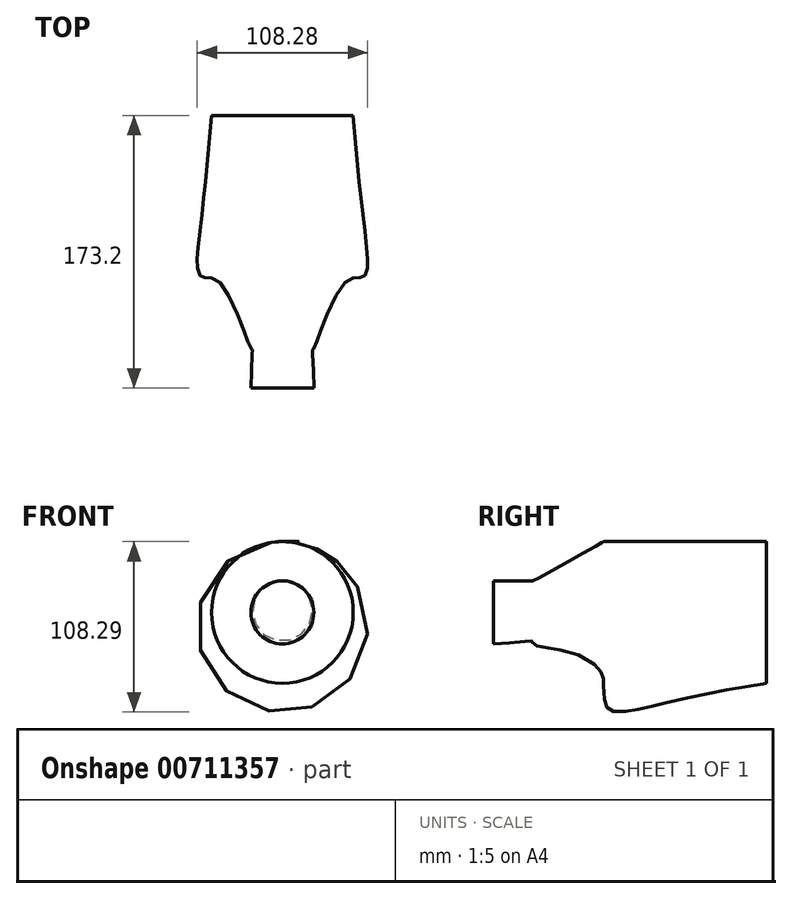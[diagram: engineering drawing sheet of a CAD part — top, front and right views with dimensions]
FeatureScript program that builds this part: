
annotation { "Feature Type Name" : "Feature", "Feature Type Description" : "" }
export const myFeature = defineFeature(function(context is Context, id is Id, definition is map)
    precondition{}
    {
        {
            var Q0;
            Q0=qCreatedBy(makeId("Front.planeOp"),FACE);
            var sketch = newSketch(context, id + "F0", { "sketchPlane" : qUnion([Q0])});
            skCircle(sketch, "E0", {"center": v(0, 45) * mm, "radius": 45 * mm});
            skSolve(sketch);
        }
        {
            var Q0;
            Q0=qCreatedBy(makeId("Front.planeOp"),FACE);
            cPlane(context, id + "F1", {"entities" : qUnion([Q0]), "cplaneType" : CPlaneType.OFFSET, "offset" : 103.3 * mm, "width" : 150 * mm, "height" : 150 * mm});
        }
        {
            var Q0;
            Q0=qCreatedBy(id+"F1.planeOp",FACE);
            var sketch = newSketch(context, id + "F2", { "sketchPlane" : qUnion([Q0])});
            skCircle(sketch, "E1.0", {"center": v(0, 45) * mm, "radius": 45 * mm});
            skSolve(sketch);
        }
        {
            var Q0;
            Q0=qCreatedBy(id+"F1.planeOp",FACE);
            cPlane(context, id + "F3", {"entities" : qUnion([Q0]), "cplaneType" : CPlaneType.OFFSET, "offset" : 44.9 * mm, "width" : 150 * mm, "height" : 150 * mm});
        }
        {
            var Q0;
            Q0=qCreatedBy(id+"F3.planeOp",FACE);
            var sketch = newSketch(context, id + "F4", { "sketchPlane" : qUnion([Q0])});
            skCircle(sketch, "E2", {"center": v(0, 45) * mm, "radius": 20 * mm});
            skSolve(sketch);
        }
        {
            var Q0;
            Q0=qCreatedBy(id+"F3.planeOp",FACE);
            cPlane(context, id + "F5", {"entities" : qUnion([Q0]), "cplaneType" : CPlaneType.OFFSET, "offset" : 25 * mm, "width" : 150 * mm, "height" : 150 * mm});
        }
        {
            var Q0;
            Q0=qCreatedBy(id+"F5.planeOp",FACE);
            var sketch = newSketch(context, id + "F6", { "sketchPlane" : qUnion([Q0])});
            skCircle(sketch, "E3.0", {"center": v(0, 45) * mm, "radius": 20 * mm});
            skSolve(sketch);
        }
        {
            var Q0;
            Q0=qCreatedBy(makeId("Right.planeOp"),FACE);
            var sketch = newSketch(context, id + "F7", { "sketchPlane" : qUnion([Q0])});
            skLineSegment(sketch, "E4.0", {"start": v(0, 0) * mm, "end": v(0, 90) * mm, "construction": true});
            skLineSegment(sketch, "E5.0", {"start": v(-103.3, 0) * mm, "end": v(-103.3, 90) * mm, "construction": true});
            skLineSegment(sketch, "E6.0", {"start": v(-148.2, 25) * mm, "end": v(-148.2, 65) * mm, "construction": true});
            skLineSegment(sketch, "E7.0", {"start": v(-173.2, 25) * mm, "end": v(-173.2, 65) * mm, "construction": true});
            skFitSpline(sketch, "E8", {"points": [v(-173.2, 65) * mm, v(-148.54, 64.98) * mm, v(-148.2, 65) * mm, v(-103.33, 89.99) * mm, v(-103.3, 90) * mm, v(0, 90) * mm], "startDerivative": vector(343.64, -0.27) * mm, "endDerivative": vector(703.29, 0) * mm});
            skSolve(sketch);
        }
        {
            var Q0;
            Q0=makeQuery(id+"F0.imprint","IMPRINT",FACE,{"disambiguationData":[TD([[makeQuery(id+"F0.imprint","IMPRINT",EDGE,{"derivedFrom":sQuery(id+"F0.wireOp",EDGE,"E0")}),1.0]])]});
            var Q1;
            Q1=makeQuery(id+"F2.imprint","IMPRINT",FACE,{"disambiguationData":[TD([[makeQuery(id+"F2.imprint","IMPRINT",EDGE,{"derivedFrom":sQuery(id+"F2.wireOp",EDGE,"E1.0")}),1.0]])]});
            var Q2;
            Q2=makeQuery(id+"F4.imprint","IMPRINT",FACE,{"disambiguationData":[TD([[makeQuery(id+"F4.imprint","IMPRINT",EDGE,{"derivedFrom":sQuery(id+"F4.wireOp",EDGE,"E2")}),1.0]])]});
            var Q3;
            Q3=makeQuery(id+"F6.imprint","IMPRINT",FACE,{"disambiguationData":[TD([[makeQuery(id+"F6.imprint","IMPRINT",EDGE,{"derivedFrom":sQuery(id+"F6.wireOp",EDGE,"E3.0")}),1.0]])]});
            var Q4;
            Q4=sQuery(id+"F7.wireOp",EDGE,"E8");
            loft(context, id + "F8", {"addGuides" : true, "sheetProfilesArray" : [{ "sheetProfileEntities" : qUnion([Q0]) }, { "sheetProfileEntities" : qUnion([Q1]) }, { "sheetProfileEntities" : qUnion([Q2]) }, { "sheetProfileEntities" : qUnion([Q3]) }], "guidesArray" : [{ "guideEntities" : qUnion([Q4]), "guideDerivativeType" : LoftGuideDerivativeType.DEFAULT, "guideDerivativeMagnitude" : 1 }]});
        }
    });
